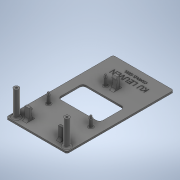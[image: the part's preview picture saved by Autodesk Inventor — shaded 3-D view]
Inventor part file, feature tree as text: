
AUTODESK INVENTOR PART (.ipt)
format: ipt  version: 2022 (Build 260153000, 153)  size: 619,008 bytes
history: native  units: mm
features: sketch x8, extrude x7, fillet x4, plane x2, mirror x1, emboss x1
ambient origin geometry x8: Origin, YZ Plane, XZ Plane, XY Plane, X Axis, Y Axis, Z Axis, Center Point
bodies: Solid1 (feature_tree)
feature tree (23):
  extrude  "Extrusion1"  Depth=127.0mm
  extrude  "Extrusion8"  Depth=4.0mm
  fillet  "Fillet3"  Radius=9.0mm
  extrude  "Extrusion9"  Depth=1.0mm
  fillet  "Fillet4"  Radius=2.5mm
  fillet  "Fillet5"  Radius=2.5mm
  plane  "Work Plane1"
  extrude  "Extrusion11"  Depth=3.0mm
  plane  "Work Plane2"
  mirror  "Mirror1"
  extrude  "Extrusion12"  Depth=2.0mm
  extrude  "Extrusion13"  Depth=29.0mm
  fillet  "Fillet6"  Radius=10.5mm
  extrude  "Extrusion14"  Depth=10.5mm
  emboss  "Emboss2"
  sketch  "Sketch1"  dims[d0=72.0mm d1=127.0mm]
  sketch  "Sketch2"  dims[d2=2.0mm d3=0.0mm d34=4.0mm d62=9.0mm d63=0.0mm]
  sketch  "Sketch8"  dims[d64=1.0mm d65=2.5mm d66=2.5mm d67=2.5mm]
  sketch  "Sketch10"  dims[d68=3.0mm d69=0.0mm d70=0.5mm]
  sketch  "Sketch11"  dims[d82=2.0mm d83=70.0mm]
  sketch  "Sketch12"  dims[d84=82.45mm d85=29.0mm d86=10.5mm]
  sketch  "Sketch13"  dims[d87=25.8mm d88=10.5mm]
  sketch  "Sketch16"  dims[d89=2.3mm d90=11.0mm d91=-16.0mm d92=10.0mm d96=1.0mm d98=3.0mm d100=2.5mm d102=1.5mm d103=3.0mm d105=5.0mm d106=0.0mm d107=10.0mm d109=2.5mm d112=3.0mm d113=3.0mm d115=5.0mm d116=0.0mm d117=10.9mm d118=1.0mm d119=1.5mm d120=10.9mm d121=5.5mm d122=82.45mm d123=27.7mm d124=50.0mm d125=30.0mm d126=50.0mm d127=4.0mm d128=6.0mm d129=6.0mm d130=6.0mm d131=6.0mm d132=6.0mm d133=30.0mm d134=0.0mm d135=2.0mm d136=2.5mm d137=2.5mm d138=10.0mm d139=0.0mm d162=5.0mm d163=1.0mm d164=0.0mm]
